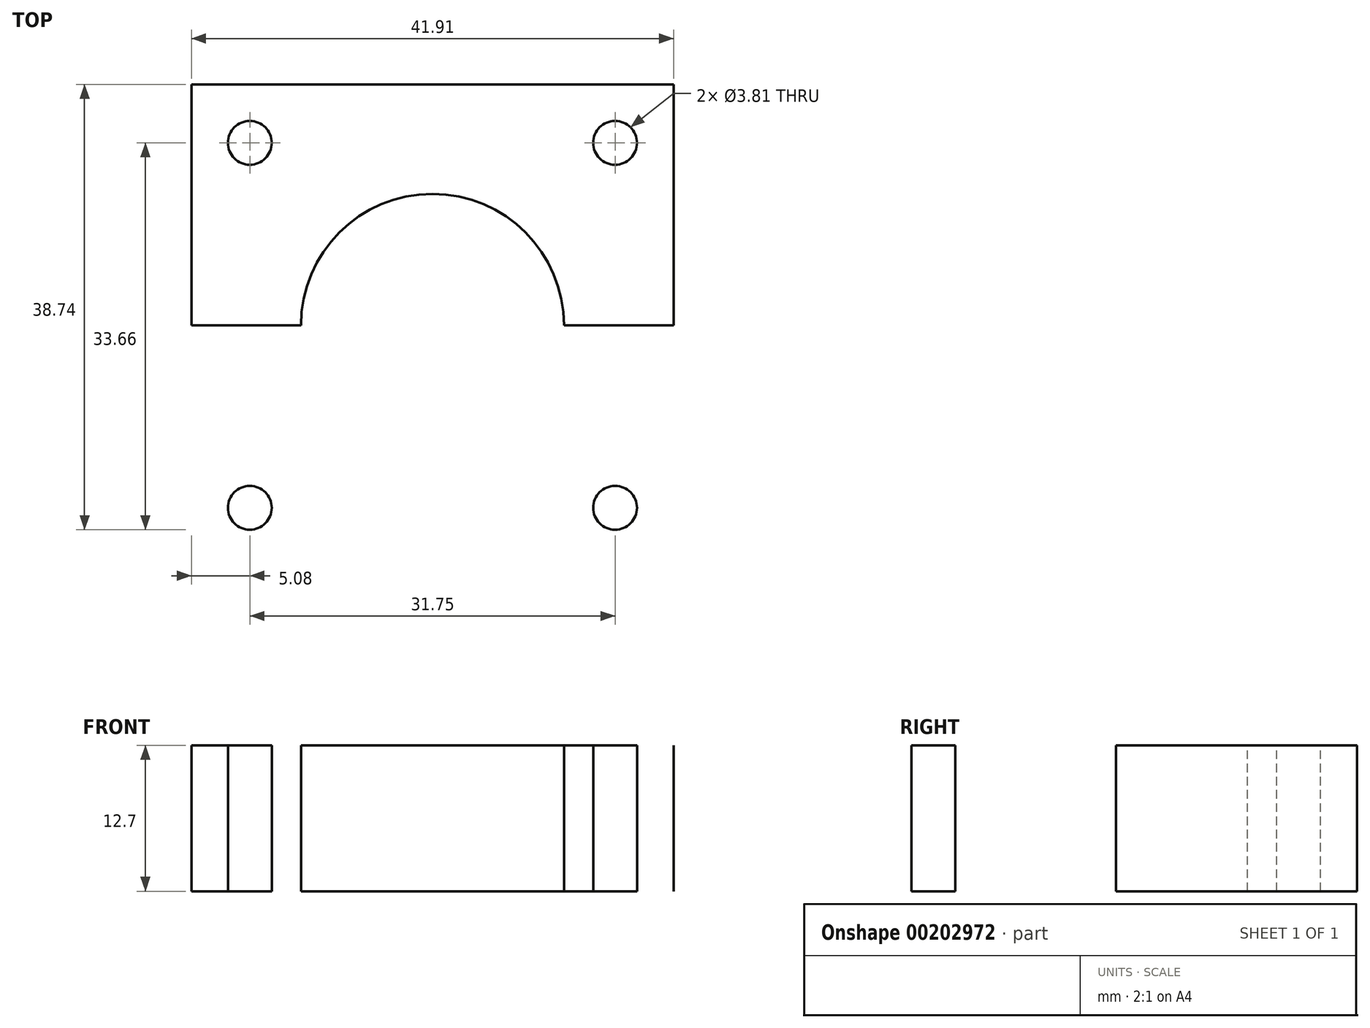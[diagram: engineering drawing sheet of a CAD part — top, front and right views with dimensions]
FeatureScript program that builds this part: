
annotation { "Feature Type Name" : "Feature", "Feature Type Description" : "" }
export const myFeature = defineFeature(function(context is Context, id is Id, definition is map)
    precondition{}
    {
        {
            var Q0;
            Q0=qCreatedBy(makeId("Top.planeOp"),FACE);
            var sketch = newSketch(context, id + "F0", { "sketchPlane" : qUnion([Q0])});
            skLineSegment(sketch, "E0.bottom", {"start": v(0, 0) * mm, "end": v(41.91, 0) * mm});
            skLineSegment(sketch, "E0.top", {"start": v(0, 41.91) * mm, "end": v(41.9, 41.91) * mm});
            skLineSegment(sketch, "E0.left", {"start": v(0, 0) * mm, "end": v(0, 41.91) * mm});
            skLineSegment(sketch, "E0.right", {"start": v(41.91, 0) * mm, "end": v(41.9, 41.91) * mm});
            skSolve(sketch);
        }
        {
            var Q0;
            Q0=makeQuery(id+"F0.imprint","IMPRINT",FACE,{"disambiguationData":[TD([[makeQuery(id+"F0.imprint","IMPRINT",EDGE,{"derivedFrom":sQuery(id+"F0.wireOp",EDGE,"E0.bottom")}),1.0]])]});
            extrude(context, id + "F1", {"entities" : qUnion([Q0]), "depth" : 12.7 * mm});
        }
        {
            var Q0;
            Q0=makeQuery(id+"F1.opExtrude","CAP_FACE",FACE,{"disambiguationData":[OSD([sQuery(id+"F0.wireOp",EDGE,"E0.bottom"),sQuery(id+"F0.wireOp",EDGE,"E0.top"),sQuery(id+"F0.wireOp",EDGE,"E0.left"),sQuery(id+"F0.wireOp",EDGE,"E0.right")])],"isStart":false});
            var sketch = newSketch(context, id + "F2", { "sketchPlane" : qUnion([Q0])});
            skLineSegment(sketch, "E1", {"start": v(0, 41.91) * mm, "end": v(5.08, 41.91) * mm});
            skLineSegment(sketch, "E2", {"start": v(5.08, 41.91) * mm, "end": v(5.08, 36.83) * mm});
            skLineSegment(sketch, "E3", {"start": v(0, 20.96) * mm, "end": v(41.91, 20.96) * mm});
            skLineSegment(sketch, "E4", {"start": v(0, 41.91) * mm, "end": v(41.91, 41.91) * mm});
            skLineSegment(sketch, "E5", {"start": v(41.91, 41.91) * mm, "end": v(41.91, 0) * mm});
            skLineSegment(sketch, "E6", {"start": v(41.91, 41.91) * mm, "end": v(36.83, 41.91) * mm});
            skLineSegment(sketch, "E7", {"start": v(36.83, 41.91) * mm, "end": v(36.83, 36.83) * mm});
            skLineSegment(sketch, "E8", {"start": v(41.91, 0) * mm, "end": v(41.91, 5.08) * mm});
            skCircle(sketch, "E9", {"center": v(36.83, 36.83) * mm, "radius": 1.9 * mm});
            skCircle(sketch, "E10", {"center": v(5.08, 36.83) * mm, "radius": 1.9 * mm});
            skCircle(sketch, "E11.MirrorC", {"center": v(36.83, 5.08) * mm, "radius": 1.9 * mm});
            skCircle(sketch, "E12.MirrorC", {"center": v(5.08, 5.08) * mm, "radius": 1.9 * mm});
            skSolve(sketch);
        }
        {
            var Q0;
            Q0=makeQuery(id+"F2.imprint","IMPRINT",FACE,{"disambiguationData":[TD([[makeQuery(id+"F2.imprint","IMPRINT",EDGE,{"derivedFrom":sQuery(id+"F2.wireOp",EDGE,"E9")}),1.0]])]});
            var Q1;
            Q1=makeQuery(id+"F2.imprint","IMPRINT",FACE,{"disambiguationData":[TD([[makeQuery(id+"F2.imprint","IMPRINT",EDGE,{"derivedFrom":sQuery(id+"F2.wireOp",EDGE,"E12.MirrorC")}),-1.0]])]});
            var Q2;
            Q2=makeQuery(id+"F2.imprint","IMPRINT",FACE,{"disambiguationData":[TD([[makeQuery(id+"F2.imprint","IMPRINT",EDGE,{"derivedFrom":sQuery(id+"F2.wireOp",EDGE,"E10")}),1.0]])]});
            var Q3;
            Q3=makeQuery(id+"F2.imprint","IMPRINT",FACE,{"disambiguationData":[TD([[makeQuery(id+"F2.imprint","IMPRINT",EDGE,{"derivedFrom":sQuery(id+"F2.wireOp",EDGE,"E11.MirrorC")}),-1.0]])]});
            extrude(context, id + "F3", {"entities" : qUnion([Q0, Q1, Q2, Q3]), "operationType" : NewBodyOperationType.REMOVE, "oppositeDirection" : true, "depth" : 25.4 * mm});
        }
        {
            var Q0;
            Q0=makeQuery(id+"F1.opExtrude","CAP_FACE",FACE,{"disambiguationData":[OSD([sQuery(id+"F0.wireOp",EDGE,"E0.bottom"),sQuery(id+"F0.wireOp",EDGE,"E0.top"),sQuery(id+"F0.wireOp",EDGE,"E0.left"),sQuery(id+"F0.wireOp",EDGE,"E0.right")])],"isStart":false});
            var sketch = newSketch(context, id + "F4", { "sketchPlane" : qUnion([Q0])});
            skLineSegment(sketch, "E13", {"start": v(0, 41.91) * mm, "end": v(20.95, 41.91) * mm});
            skLineSegment(sketch, "E14", {"start": v(20.95, 41.91) * mm, "end": v(20.95, 20.96) * mm});
            skCircle(sketch, "E15", {"center": v(20.95, 20.96) * mm, "radius": 11.43 * mm});
            skSolve(sketch);
        }
        {
            var Q0;
            Q0 = qSketchRegion(id + "F4", true);
            extrude(context, id + "F5", {"entities" : qUnion([Q0]), "operationType" : NewBodyOperationType.REMOVE, "endBound" : BoundingType.THROUGH_ALL, "oppositeDirection" : true, "depth" : 25.4 * mm});
        }
    });
